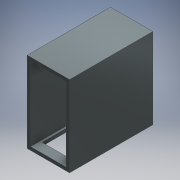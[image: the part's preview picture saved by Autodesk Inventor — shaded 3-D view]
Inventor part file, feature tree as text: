
AUTODESK INVENTOR PART (.ipt)
format: ipt  version: 2016 (Build 200138000, 138)  size: 162,816 bytes
history: native  units: mm
features: sketch x6, extrude x5
ambient origin geometry x8: Origin, YZ Plane, XZ Plane, XY Plane, X Axis, Y Axis, Z Axis, Center Point
bodies: Solid1 (feature_tree)
feature tree (11):
  extrude  "Extrusion1"  Depth=520.0mm
  extrude  "Extrusion2"  Depth=583.0mm TaperAngle=0.0deg
  extrude  "Extrusion3"  Depth=440.0mm
  sketch  "Sketch4"  dims[d7=77.0mm d8=38.0mm]
  extrude  "Extrusion4"  Depth=38.0mm
  extrude  "Extrusion5"  Depth=70.0mm
  sketch  "Sketch1"  dims[d0=250.0mm d1=520.0mm]
  sketch  "Sketch2"  dims[d2=23.0mm d3=583.0mm d4=0.0mm]
  sketch  "Sketch3"  dims[d5=220.0mm d6=440.0mm]
  sketch  "Sketch5"  dims[d9=583.0mm d10=0.0mm d11=70.0mm]
  sketch  "Sketch6"  dims[d12=80.0mm d13=430.0mm d14=143.0mm d15=583.0mm d16=0.0mm d17=47.0mm d18=583.0mm d19=0.0mm d20=16.0mm d21=170.0mm d22=45.0mm d23=16.0mm d24=170.0mm d25=45.0mm d26=10.0mm d27=0.0mm]
